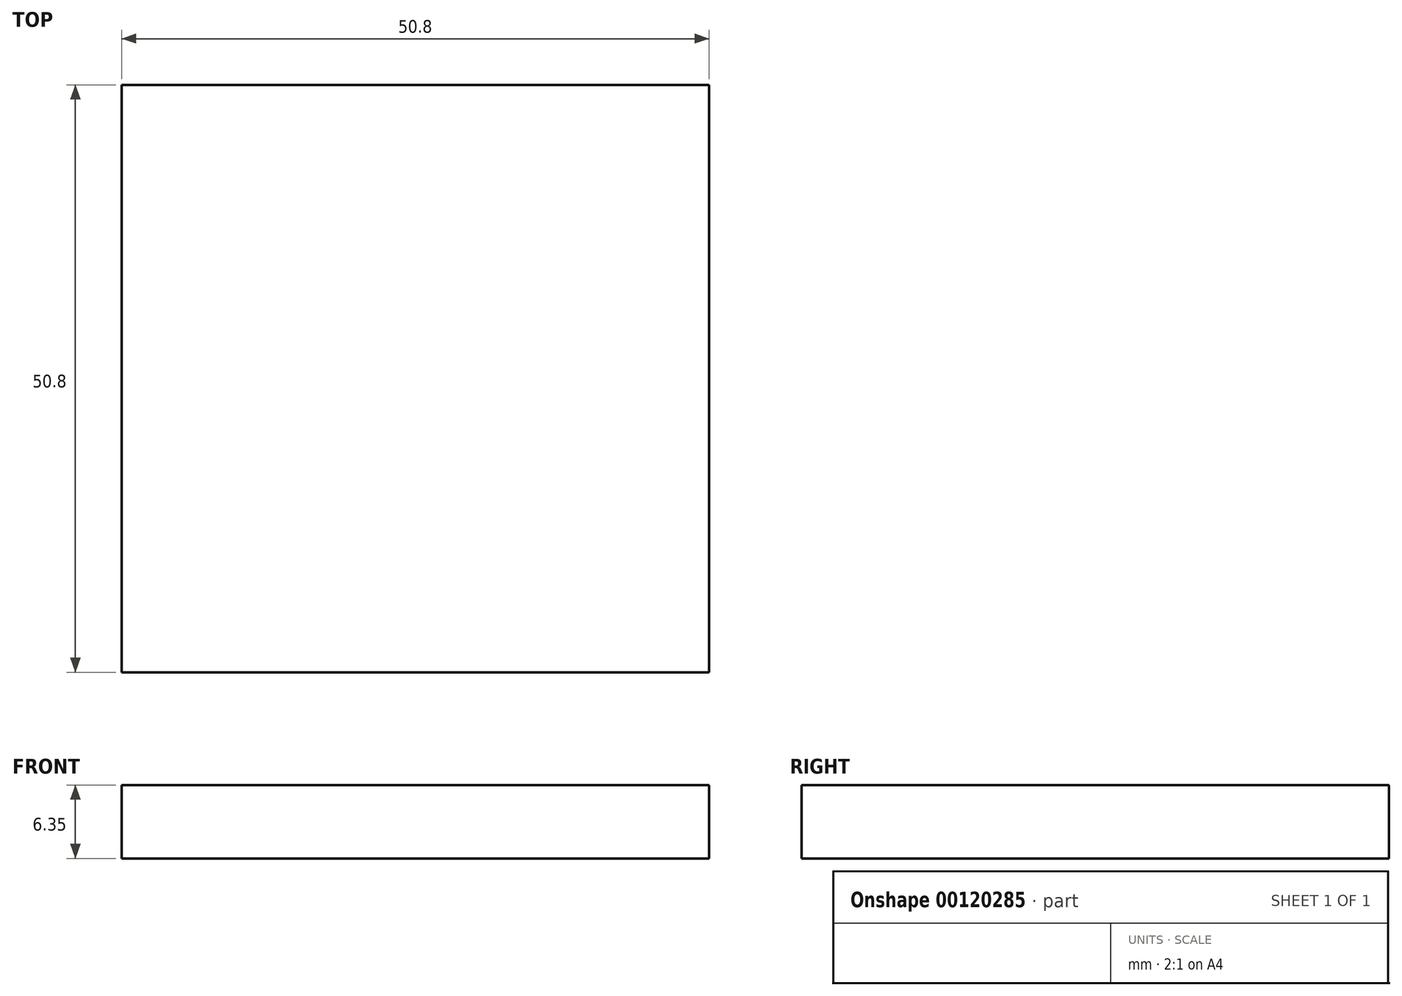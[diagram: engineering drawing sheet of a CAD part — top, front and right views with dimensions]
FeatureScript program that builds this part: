
annotation { "Feature Type Name" : "Feature", "Feature Type Description" : "" }
export const myFeature = defineFeature(function(context is Context, id is Id, definition is map)
    precondition{}
    {
        {
            var Q0;
            Q0=qCreatedBy(makeId("Top.planeOp"),FACE);
            var sketch = newSketch(context, id + "F0", { "sketchPlane" : qUnion([Q0])});
            skLineSegment(sketch, "E0.bottom", {"start": v(-27.7, 31.85) * mm, "end": v(23.1, 31.85) * mm});
            skLineSegment(sketch, "E0.top", {"start": v(-27.7, -18.95) * mm, "end": v(23.1, -18.95) * mm});
            skLineSegment(sketch, "E0.left", {"start": v(-27.7, 31.85) * mm, "end": v(-27.7, -18.95) * mm});
            skLineSegment(sketch, "E0.right", {"start": v(23.1, 31.85) * mm, "end": v(23.1, -18.95) * mm});
            skSolve(sketch);
        }
        {
            var Q0;
            Q0 = qSketchRegion(id + "F0", true);
            extrude(context, id + "F1", {"entities" : qUnion([Q0]), "depth" : 6.35 * mm});
        }
    });
